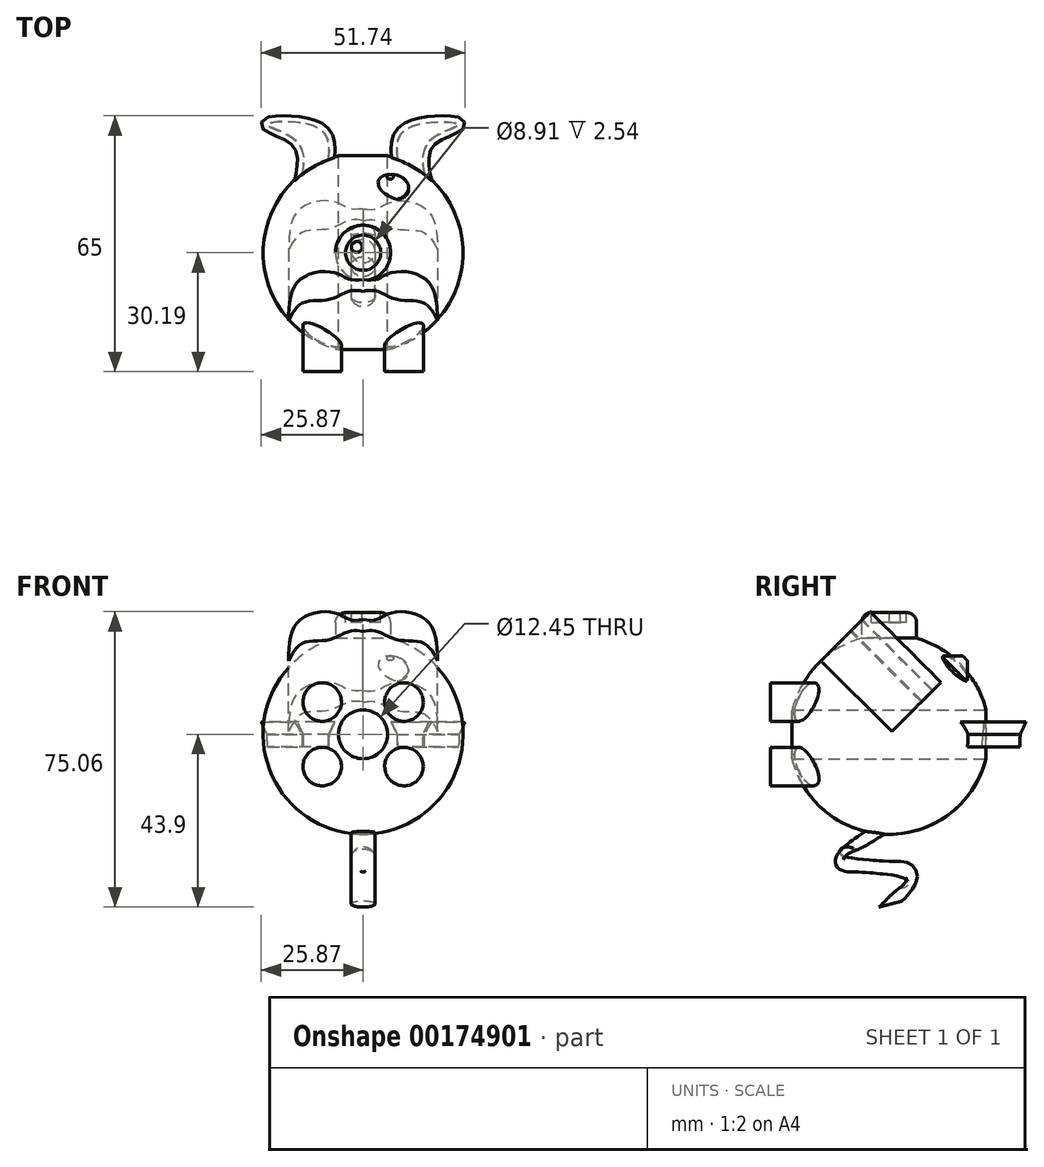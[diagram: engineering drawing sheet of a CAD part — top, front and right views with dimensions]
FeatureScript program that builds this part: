
annotation { "Feature Type Name" : "Feature", "Feature Type Description" : "" }
export const myFeature = defineFeature(function(context is Context, id is Id, definition is map)
    precondition{}
    {
        {
            var Q0;
            Q0=qCreatedBy(makeId("Front.planeOp"),FACE);
            var sketch = newSketch(context, id + "F0", { "sketchPlane" : qUnion([Q0])});
            skCircle(sketch, "E0", {"center": v(0, 0) * mm, "radius": 25.4 * mm});
            skSolve(sketch);
        }
        {
            var Q0;
            Q0=qSketchRegion(id+"F0",true);
            extrude(context, id + "F1", {"entities" : qUnion([Q0]), "depth" : 25.4 * mm});
        }
        {
            var Q0;
            Q0=makeQuery(id+"F1.opExtrude","CAP_EDGE",EDGE,{"disambiguationData":[OSD([sQuery(id+"F0.wireOp",EDGE,"E0")])],"isStart":false});
            fillet(context, id + "F2", {"entities" : qUnion([Q0]), "radius" : 25.4 * mm, "tangentPropagation" : true, "allowEdgeOverflow" : false});
        }
        {
            var Q0;
            Q0=makeQuery(id+"F1.opExtrude","SWEPT_BODY",BODY,{"disambiguationData":[OSD([sQuery(id+"F0.wireOp",EDGE,"E0")])]});
            var Q1;
            Q1=qCreatedBy(makeId("Front.planeOp"),FACE);
            mirror(context, id + "F3", {"operationType" : NewBodyOperationType.ADD, "entities" : qUnion([Q0]), "mirrorPlane" : qUnion([Q1])});
        }
        {
            var Q0;
            Q0=qCreatedBy(makeId("Top.planeOp"),FACE);
            cPlane(context, id + "F4", {"entities" : qUnion([Q0]), "cplaneType" : CPlaneType.OFFSET, "offset" : 25.4 * mm, "width" : 152.4 * mm, "height" : 152.4 * mm});
        }
        {
            var Q0;
            Q0=qCreatedBy(id+"F4.planeOp",FACE);
            var sketch = newSketch(context, id + "F5", { "sketchPlane" : qUnion([Q0])});
            skCircle(sketch, "E1", {"center": v(0, 0) * mm, "radius": 7 * mm});
            skSolve(sketch);
        }
        {
            var Q0;
            Q0=qSketchRegion(id+"F5",true);
            extrude(context, id + "F6", {"entities" : qUnion([Q0]), "operationType" : NewBodyOperationType.ADD, "depth" : 5.52 * mm, "hasSecondDirection" : true, "secondDirectionOppositeDirection" : true, "secondDirectionDepth" : 25.4 * mm});
        }
        {
            var Q0;
            Q0=makeQuery(id+"F6.opExtrude","CAP_EDGE",EDGE,{"disambiguationData":[OSD([sQuery(id+"F5.wireOp",EDGE,"E1")])],"isStart":false});
            fillet(context, id + "F7", {"entities" : qUnion([Q0]), "radius" : 2.54 * mm, "tangentPropagation" : true, "allowEdgeOverflow" : false});
        }
        {
            var Q0;
            Q0=makeQuery(id+"F6.opExtrude","CAP_FACE",FACE,{"disambiguationData":[OSD([sQuery(id+"F5.wireOp",EDGE,"E1")])],"isStart":false});
            var sketch = newSketch(context, id + "F8", { "sketchPlane" : qUnion([Q0])});
            skCircle(sketch, "E2", {"center": v(1.6, 1.46) * mm, "radius": 1.37 * mm});
            skLineSegment(sketch, "E3", {"start": v(0, 0) * mm, "end": v(0, -5.07) * mm, "construction": true});
            skCircle(sketch, "E4.MirrorC", {"center": v(-1.6, 1.46) * mm, "radius": 1.37 * mm});
            skSolve(sketch);
        }
        {
            var Q0;
            Q0=makeQuery(id+"F8.imprint","IMPRINT",FACE,{"disambiguationData":[TD([[makeQuery(id+"F8.imprint","IMPRINT",EDGE,{"derivedFrom":sQuery(id+"F8.wireOp",EDGE,"E2")}),1.0]])]});
            var Q1;
            Q1=makeQuery(id+"F8.imprint","IMPRINT",FACE,{"disambiguationData":[TD([[makeQuery(id+"F8.imprint","IMPRINT",EDGE,{"derivedFrom":sQuery(id+"F8.wireOp",EDGE,"E4.MirrorC")}),-1.0]])]});
            extrude(context, id + "F9", {"entities" : qUnion([Q0, Q1]), "operationType" : NewBodyOperationType.REMOVE, "oppositeDirection" : true, "depth" : 2.54 * mm});
        }
        {
            var Q0;
            Q0=qCreatedBy(makeId("Front.planeOp"),FACE);
            cPlane(context, id + "F10", {"entities" : qUnion([Q0]), "cplaneType" : CPlaneType.OFFSET, "offset" : 25.4 * mm, "width" : 152.4 * mm, "height" : 152.4 * mm});
        }
        {
            var Q0;
            Q0=qCreatedBy(id+"F10.planeOp",FACE);
            var sketch = newSketch(context, id + "F11", { "sketchPlane" : qUnion([Q0])});
            skCircle(sketch, "E5", {"center": v(10.4, 8.2) * mm, "radius": 4.9 * mm});
            skLineSegment(sketch, "E6", {"start": v(0, 0) * mm, "end": v(0, 17.66) * mm, "construction": true});
            skLineSegment(sketch, "E7", {"start": v(0, 0) * mm, "end": v(18.01, 0) * mm, "construction": true});
            skCircle(sketch, "E8.MirrorC", {"center": v(-10.4, 8.2) * mm, "radius": 4.9 * mm});
            skLineSegment(sketch, "E9.MirrorCS", {"start": v(0, 0) * mm, "end": v(-18.01, 0) * mm, "construction": true});
            skCircle(sketch, "E10.MirrorC", {"center": v(10.4, -8.2) * mm, "radius": 4.9 * mm});
            skCircle(sketch, "E11.MirrorC", {"center": v(-10.4, -8.2) * mm, "radius": 4.9 * mm});
            skSolve(sketch);
        }
        {
            var Q0;
            Q0=qSketchRegion(id+"F11",true);
            extrude(context, id + "F12", {"entities" : qUnion([Q0]), "operationType" : NewBodyOperationType.ADD, "depth" : 4.8 * mm, "hasSecondDirection" : true, "secondDirectionOppositeDirection" : true, "secondDirectionDepth" : 25.4 * mm});
        }
        {
            var Q0;
            Q0=qCreatedBy(makeId("Top.planeOp"),FACE);
            cPlane(context, id + "F13", {"entities" : qUnion([Q0]), "cplaneType" : CPlaneType.OFFSET, "offset" : 22.86 * mm, "oppositeDirection" : true, "width" : 152.4 * mm, "height" : 152.4 * mm});
        }
        {
            var Q0;
            Q0=qCreatedBy(id+"F13.planeOp",FACE);
            var sketch = newSketch(context, id + "F14", { "sketchPlane" : qUnion([Q0])});
            skCircle(sketch, "E12", {"center": v(0, 0) * mm, "radius": 3.03 * mm});
            skSolve(sketch);
        }
        {
            var Q0;
            Q0=qCreatedBy(makeId("Right.planeOp"),FACE);
            var sketch = newSketch(context, id + "F15", { "sketchPlane" : qUnion([Q0])});
            skFitSpline(sketch, "E13", {"points": [v(0, -22.61) * mm, v(-11.24, -32.4) * mm, v(4.1, -35.62) * mm, v(0, -43.24) * mm], "startDerivative": vector(-55.1, -33.68) * mm, "endDerivative": vector(-32.28, -33.35) * mm});
            skSolve(sketch);
        }
        {
            var Q0;
            Q0=qSketchRegion(id+"F14",true);
            var Q1;
            Q1=qConstructionFilter(qBodyType(qCreatedBy(id+"F15",EDGE),BodyType.WIRE),ConstructionObject.NO);
            sweep(context, id + "F16", {"operationType" : NewBodyOperationType.ADD, "profiles" : qUnion([Q0]), "path" : qUnion([Q1])});
        }
        {
            var Q0;
            Q0=qCreatedBy(makeId("Right.planeOp"),FACE);
            var Q1;
            Q1=qCreatedBy(makeId("Front.planeOp"),FACE);
            cPlane(context, id + "F17", {"entities" : qUnion([Q0, Q1]), "cplaneType" : CPlaneType.MID_PLANE, "offset" : 152.4 * mm, "width" : 152.4 * mm, "height" : 152.4 * mm});
        }
        {
            var Q0;
            Q0=qCreatedBy(id+"F17.planeOp",FACE);
            var Q1;
            Q1=qCreatedBy(makeId("Front.planeOp"),FACE);
            cPlane(context, id + "F18", {"entities" : qUnion([Q0, Q1]), "cplaneType" : CPlaneType.MID_PLANE, "offset" : 25.4 * mm, "width" : 152.4 * mm, "height" : 152.4 * mm});
        }
        {
            var Q0;
            Q0=qCreatedBy(makeId("Top.planeOp"),FACE);
            var sketch = newSketch(context, id + "F19", { "sketchPlane" : qUnion([Q0])});
            skFitSpline(sketch, "E14", {"points": [v(8.87, 22.6) * mm, v(11.2, 31.67) * mm, v(24.38, 32.63) * mm, v(17.04, 28.44) * mm, v(16.14, 17.25) * mm], "startDerivative": vector(-5.6, 45.85) * mm, "endDerivative": vector(10.96, -49.38) * mm});
            skLineSegment(sketch, "E15", {"start": v(8.87, 22.6) * mm, "end": v(16.14, 17.25) * mm});
            skLineSegment(sketch, "E16", {"start": v(0, 20.96) * mm, "end": v(0, 38.12) * mm, "construction": true});
            skFitSpline(sketch, "E17.MirrorCS", {"points": [v(-8.87, 22.6) * mm, v(-11.2, 31.67) * mm, v(-24.38, 32.63) * mm, v(-17.04, 28.44) * mm, v(-16.14, 17.25) * mm], "startDerivative": vector(5.6, 45.85) * mm, "endDerivative": vector(-10.96, -49.38) * mm});
            skLineSegment(sketch, "E18.MirrorCS", {"start": v(-8.87, 22.6) * mm, "end": v(-16.14, 17.25) * mm});
            skSolve(sketch);
        }
        {
            var Q0;
            Q0=qSketchRegion(id+"F19",true);
            extrude(context, id + "F20", {"entities" : qUnion([Q0]), "operationType" : NewBodyOperationType.ADD, "depth" : 3.17 * mm, "hasDraft" : true, "draftAngle" : 25 * degree, "hasSecondDirection" : true, "secondDirectionOppositeDirection" : true, "secondDirectionDepth" : 3.17 * mm, "hasSecondDirectionDraft" : true, "secondDirectionDraftAngle" : 2 * degree, "secondDirectionDraftPullDirection" : true});
        }
        {
            var Q0;
            Q0=qCreatedBy(makeId("Top.planeOp"),FACE);
            var Q1;
            Q1=qCreatedBy(makeId("Front.planeOp"),FACE);
            cPlane(context, id + "F21", {"entities" : qUnion([Q0, Q1]), "cplaneType" : CPlaneType.MID_PLANE, "offset" : 152.4 * mm, "width" : 152.4 * mm, "height" : 152.4 * mm});
        }
        {
            var Q0;
            Q0=qCreatedBy(id+"F21.planeOp",FACE);
            cPlane(context, id + "F22", {"entities" : qUnion([Q0]), "cplaneType" : CPlaneType.OFFSET, "offset" : 25.4 * mm, "width" : 152.4 * mm, "height" : 152.4 * mm});
        }
        {
            var Q0;
            Q0=qCreatedBy(id+"F22.planeOp",FACE);
            var sketch = newSketch(context, id + "F23", { "sketchPlane" : qUnion([Q0])});
            skCircle(sketch, "E19", {"center": v(-6.9, 0) * mm, "radius": 4.66 * mm});
            skLineSegment(sketch, "E20", {"start": v(0, 4.8) * mm, "end": v(0, -4.32) * mm, "construction": true});
            skCircle(sketch, "E21.MirrorC", {"center": v(6.9, 0) * mm, "radius": 4.66 * mm});
            skSolve(sketch);
        }
        {
            var Q0;
            Q0=makeQuery(id+"F23.imprint","IMPRINT",FACE,{"disambiguationData":[TD([[makeQuery(id+"F23.imprint","IMPRINT",EDGE,{"derivedFrom":sQuery(id+"F23.wireOp",EDGE,"E21.MirrorC")}),-1.0]])]});
            var Q1;
            Q1=makeQuery(id+"F23.imprint","IMPRINT",FACE,{"disambiguationData":[TD([[makeQuery(id+"F23.imprint","IMPRINT",EDGE,{"derivedFrom":sQuery(id+"F23.wireOp",EDGE,"E19")}),1.0]])]});
            extrude(context, id + "F24", {"entities" : qUnion([Q0, Q1]), "operationType" : NewBodyOperationType.ADD, "depth" : 1.91 * mm, "hasSecondDirection" : true, "secondDirectionOppositeDirection" : true, "secondDirectionDepth" : 25.4 * mm});
        }
        {
            var Q0;
            Q0=makeQuery(id+"F24.opExtrude","CAP_EDGE",EDGE,{"disambiguationData":[OSD([sQuery(id+"F23.wireOp",EDGE,"E21.MirrorC")])],"isStart":false});
            var Q1;
            Q1=makeQuery(id+"F24.opExtrude","CAP_EDGE",EDGE,{"disambiguationData":[OSD([sQuery(id+"F23.wireOp",EDGE,"E19")])],"isStart":false});
            chamfer(context, id + "F25", {"entities" : qUnion([Q0, Q1]), "width" : 3.8 * mm, "tangentPropagation" : true});
        }
        {
            var Q0;
            Q0=qCreatedBy(id+"F22.planeOp",FACE);
            var sketch = newSketch(context, id + "F26", { "sketchPlane" : qUnion([Q0])});
            skLineSegment(sketch, "E22", {"start": v(-2.38, -7.16) * mm, "end": v(-2.38, -2.32) * mm});
            skLineSegment(sketch, "E23", {"start": v(-2.38, -2.32) * mm, "end": v(-5.83, -6.43) * mm});
            skLineSegment(sketch, "E24", {"start": v(-5.83, -6.43) * mm, "end": v(-10.51, -7.94) * mm});
            skLineSegment(sketch, "E25", {"start": v(-10.51, -7.94) * mm, "end": v(-12.35, -9.65) * mm});
            skLineSegment(sketch, "E26", {"start": v(-12.35, -9.65) * mm, "end": v(-9.5, -9.65) * mm});
            skLineSegment(sketch, "E27", {"start": v(-9.5, -9.65) * mm, "end": v(-2.38, -7.16) * mm});
            skLineSegment(sketch, "E28", {"start": v(0, 0) * mm, "end": v(0, -9.78) * mm, "construction": true});
            skLineSegment(sketch, "E29.MirrorCS", {"start": v(2.38, -2.32) * mm, "end": v(5.83, -6.43) * mm});
            skLineSegment(sketch, "E30.MirrorCS", {"start": v(2.38, -7.16) * mm, "end": v(2.38, -2.32) * mm});
            skLineSegment(sketch, "E31.MirrorCS", {"start": v(9.5, -9.65) * mm, "end": v(2.38, -7.16) * mm});
            skLineSegment(sketch, "E32.MirrorCS", {"start": v(5.83, -6.43) * mm, "end": v(10.51, -7.94) * mm});
            skLineSegment(sketch, "E33.MirrorCS", {"start": v(10.51, -7.94) * mm, "end": v(12.35, -9.65) * mm});
            skLineSegment(sketch, "E34.MirrorCS", {"start": v(12.35, -9.65) * mm, "end": v(9.5, -9.65) * mm});
            skSolve(sketch);
        }
        {
            var Q0;
            Q0=qSketchRegion(id+"F26",true);
            extrude(context, id + "F27", {"entities" : qUnion([Q0]), "oppositeDirection" : true, "depth" : 25.4 * mm});
        }
        {
            var Q0;
            Q0=qCreatedBy(makeId("Front.planeOp"),FACE);
            var Q1;
            Q1=qCreatedBy(makeId("Top.planeOp"),FACE);
            cPlane(context, id + "F28", {"entities" : qUnion([Q0, Q1]), "cplaneType" : CPlaneType.MID_PLANE, "offset" : 152.4 * mm, "flipAlignment" : true, "width" : 152.4 * mm, "height" : 152.4 * mm});
        }
        {
            var Q0;
            Q0=qCreatedBy(id+"F28.planeOp",FACE);
            cPlane(context, id + "F29", {"entities" : qUnion([Q0]), "cplaneType" : CPlaneType.OFFSET, "offset" : 25.4 * mm, "width" : 152.4 * mm, "height" : 152.4 * mm});
        }
        {
            var Q0;
            Q0=qCreatedBy(id+"F29.planeOp",FACE);
            var sketch = newSketch(context, id + "F30", { "sketchPlane" : qUnion([Q0])});
            skLineSegment(sketch, "E35", {"start": v(0, 0) * mm, "end": v(0, 15.77) * mm, "construction": true});
            skFitSpline(sketch, "E36", {"points": [v(0, 15.77) * mm, v(3.27, 15.77) * mm, v(6.06, 17.68) * mm, v(11, 18.56) * mm, v(16.83, 14.56) * mm, v(18.95, 0.98) * mm], "startDerivative": vector(23.56, -3.59) * mm, "endDerivative": vector(1.15, -51.26) * mm});
            skFitSpline(sketch, "E37", {"points": [v(0, 11.54) * mm, v(3.38, 11.67) * mm, v(8.7, 8.57) * mm, v(14.98, 7.62) * mm, v(18.95, 0.98) * mm], "startDerivative": vector(17.37, 4.43) * mm, "endDerivative": vector(10.69, -29.34) * mm});
            skFitSpline(sketch, "E38.MirrorCS", {"points": [v(0, 15.77) * mm, v(-3.27, 15.77) * mm, v(-6.06, 17.68) * mm, v(-11, 18.56) * mm, v(-16.83, 14.56) * mm, v(-18.95, 0.98) * mm], "startDerivative": vector(-23.56, -3.59) * mm, "endDerivative": vector(-1.15, -51.26) * mm});
            skFitSpline(sketch, "E39.MirrorCS", {"points": [v(0, 11.54) * mm, v(-3.38, 11.67) * mm, v(-8.7, 8.57) * mm, v(-14.98, 7.62) * mm, v(-18.95, 0.98) * mm], "startDerivative": vector(-17.37, 4.43) * mm, "endDerivative": vector(-10.69, -29.34) * mm});
            skSolve(sketch);
        }
        {
            var Q0;
            Q0=qSketchRegion(id+"F30",true);
            extrude(context, id + "F31", {"entities" : qUnion([Q0]), "oppositeDirection" : true, "depth" : 25.4 * mm});
        }
        {
            var Q0;
            Q0=qCreatedBy(makeId("Front.planeOp"),FACE);
            cPlane(context, id + "F32", {"entities" : qUnion([Q0]), "cplaneType" : CPlaneType.OFFSET, "offset" : 25.4 * mm, "oppositeDirection" : true, "width" : 152.4 * mm, "height" : 152.4 * mm});
        }
        {
            var Q0;
            Q0=qCreatedBy(id+"F32.planeOp",FACE);
            var sketch = newSketch(context, id + "F33", { "sketchPlane" : qUnion([Q0])});
            skPoint(sketch, "E40", {"position": v(0, 0) * mm});
            skSolve(sketch);
        }
        {
            var Q0;
            Q0=sQuery(id+"F33.wireOp",VERTEX,"E40");
            var Q1;
            Q1=makeQuery(id+"F1.opExtrude","SWEPT_BODY",BODY,{"disambiguationData":[OSD([sQuery(id+"F0.wireOp",EDGE,"E0")])]});
            hole(context, id + "F34", {"style" : HoleStyle.SIMPLE, "endStyle" : HoleEndStyle.THROUGH, "oppositeDirection" : true, "holeDiameter" : 12.45 * mm, "locations" : qUnion([Q0]), "scope" : qUnion([Q1]), "isTappedThrough" : true});
        }
        {
            var Q0;
            Q0=makeQuery(id+"F27.opExtrude","SWEPT_BODY",BODY,{"disambiguationData":[OSD([sQuery(id+"F26.wireOp",EDGE,"E29.MirrorCS"),sQuery(id+"F26.wireOp",EDGE,"E30.MirrorCS"),sQuery(id+"F26.wireOp",EDGE,"E31.MirrorCS"),sQuery(id+"F26.wireOp",EDGE,"E32.MirrorCS"),sQuery(id+"F26.wireOp",EDGE,"E33.MirrorCS"),sQuery(id+"F26.wireOp",EDGE,"E34.MirrorCS")])]});
            deleteBodies(context, id + "F35", {"entities" : qUnion([Q0])});
        }
        {
            var Q0;
            Q0=makeQuery(id+"F27.opExtrude","SWEPT_BODY",BODY,{"disambiguationData":[OSD([sQuery(id+"F26.wireOp",EDGE,"E22"),sQuery(id+"F26.wireOp",EDGE,"E23"),sQuery(id+"F26.wireOp",EDGE,"E24"),sQuery(id+"F26.wireOp",EDGE,"E25"),sQuery(id+"F26.wireOp",EDGE,"E26"),sQuery(id+"F26.wireOp",EDGE,"E27")])]});
            deleteBodies(context, id + "F36", {"entities" : qUnion([Q0])});
        }
        {
            var Q0;
            Q0=makeQuery(id+"F1.opExtrude","SWEPT_BODY",BODY,{"disambiguationData":[OSD([sQuery(id+"F0.wireOp",EDGE,"E0")])]});
            var Q1;
            Q1=sQuery(id+"F11.wireOp",VERTEX,"E6.start");
            transform(context, id + "F37", {"entities" : qUnion([Q0]), "transformType" : TransformType.SCALE_UNIFORMLY, "scale" : 1, "scalePoint" : qUnion([Q1]), "makeCopy" : false});
        }
    });
